# Revit family: Void Error
name_source: partatom
category: Generic Models
revit_build: Autodesk Revit 2018 (Build: 20170927_1515(x64)
units: mm (PartAtom-declared; Revit-internal decimal feet)

## family parameters
Always vertical = Yes
Can host rebar = No
Cut with Voids When Loaded = No
Part Type = Normal
Room Calculation Point = No
Round Connector Dimension = Use Diameter
Shared = No
Work Plane-Based = Yes

## types (1)
- Void Error
    Column Material = <By Category>
    Default Elevation = 4' - 0"
    Footign Material = <By Category>
    Panel - Depth of Adjoining plus Joint = 0' - 10"
    Panel - TO Adjoining Panel = 40' - 9"
    Panel Coping Material = <By Category>
    Panel Depth = 0' - 9 1/4"
    Panel Height Above Grade = 41' - 11"
    Panel Height Below Grade = 1' - 0"
    Panel Material = <By Category>
    Panel Width - Left = 16' - 3"
    Panel Width Right = 16' - 3"
    Reveal 1 - BO = 9' - 10 3/4"
    Reveal 2 - TO = 11' - 2 3/4"
    Reveal 3 - BO = 26' - 11"
    Reveal 4 - TO = 28' - 3"
    Reveal 5 - BO = 33' - 5"
    Reveal 6 - TO = 34' - 7"
    Reveal 7 - BO = 39' - 7"
    Top of Fin = 23' - 6"
    Top of Fin - Offset Down Cut = 1' - 0"
    Width = 75' - 0"
    Wood Blocking Material = <By Category>

## geometry (parser evidence)
native form markers: Blend x4, Sweep x3
no freeform markers — native parametric forms only
